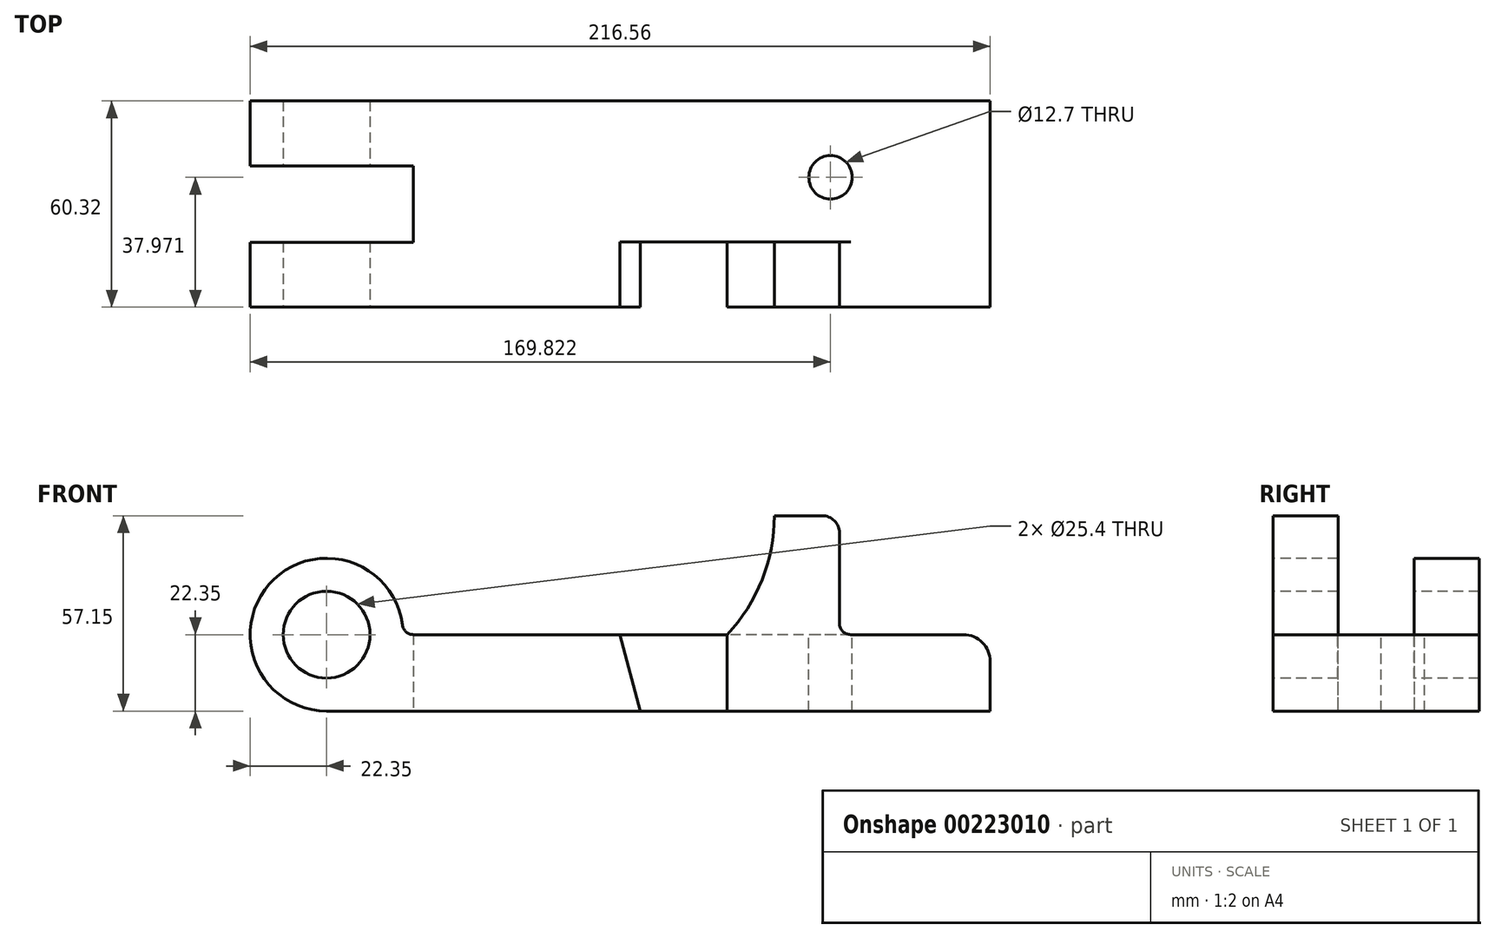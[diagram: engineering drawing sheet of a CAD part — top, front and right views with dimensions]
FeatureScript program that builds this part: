
annotation { "Feature Type Name" : "Feature", "Feature Type Description" : "" }
export const myFeature = defineFeature(function(context is Context, id is Id, definition is map)
    precondition{}
    {
        {
            var Q0;
            Q0=qCreatedBy(makeId("Front.planeOp"),FACE);
            var sketch = newSketch(context, id + "F0", { "sketchPlane" : qUnion([Q0])});
            skCircle(sketch, "E0", {"center": v(0, 0) * mm, "radius": 12.7 * mm});
            skArc(sketch, "E1", {"start": v(22.17, 2.88) * mm, "mid": v(-16.8, 14.75) * mm, "end": v(0, -22.35) * mm});
            skLineSegment(sketch, "E2", {"start": v(0, 0) * mm, "end": v(-22.35, 0) * mm, "construction": true});
            skLineSegment(sketch, "E3", {"start": v(-22.35, 0) * mm, "end": v(-22.35, -22.35) * mm, "construction": true});
            skLineSegment(sketch, "E4", {"start": v(194.2, -22.35) * mm, "end": v(194.2, -7.87) * mm});
            skLineSegment(sketch, "E5", {"start": v(0, 0) * mm, "end": v(0, -22.35) * mm, "construction": true});
            skLineSegment(sketch, "E6", {"start": v(0, -22.35) * mm, "end": v(-22.35, -22.35) * mm, "construction": true});
            skLineSegment(sketch, "E7", {"start": v(0, -22.35) * mm, "end": v(91.85, -22.35) * mm});
            skLineSegment(sketch, "E8", {"start": v(91.85, -22.35) * mm, "end": v(117.25, -22.35) * mm});
            skLineSegment(sketch, "E9", {"start": v(117.25, -22.35) * mm, "end": v(194.2, -22.35) * mm});
            skLineSegment(sketch, "E10", {"start": v(91.85, -22.35) * mm, "end": v(85.85, 0) * mm});
            skLineSegment(sketch, "E11", {"start": v(117.25, -22.35) * mm, "end": v(117.25, 0) * mm});
            skLineSegment(sketch, "E12", {"start": v(186.33, 0) * mm, "end": v(153.4, 0) * mm});
            skLineSegment(sketch, "E13", {"start": v(85.85, 0) * mm, "end": v(25.44, 0) * mm});
            skLineSegment(sketch, "E14", {"start": v(85.85, 0) * mm, "end": v(117.25, 0) * mm});
            skPoint(sketch, "E15.visualSharp", {"position": v(22.35, 0) * mm});
            skArc(sketch, "E15.filletArc", {"start": v(22.17, 2.88) * mm, "mid": v(23.26, 0.82) * mm, "end": v(25.44, 0) * mm});
            skLineSegment(sketch, "E16", {"start": v(0, 0) * mm, "end": v(0, 34.8) * mm, "construction": true});
            skLineSegment(sketch, "E17", {"start": v(0, 34.8) * mm, "end": v(145, 34.8) * mm, "construction": true});
            skLineSegment(sketch, "E18", {"start": v(150.09, 29.72) * mm, "end": v(150.09, 3.3) * mm});
            skLineSegment(sketch, "E19", {"start": v(131.04, 34.8) * mm, "end": v(131.04, 0) * mm, "construction": true});
            skLineSegment(sketch, "E20", {"start": v(150.09, 29.72) * mm, "end": v(150.09, 3.3) * mm, "construction": true});
            skPoint(sketch, "E21.visualSharp", {"position": v(150.09, 34.8) * mm});
            skArc(sketch, "E21.filletArc", {"start": v(150.09, 29.72) * mm, "mid": v(148.6, 33.31) * mm, "end": v(145, 34.8) * mm});
            skPoint(sketch, "E22.newPointA", {"position": v(150.09, -22.35) * mm});
            skArc(sketch, "E22.filletArc", {"start": v(150.09, 3.3) * mm, "mid": v(151.06, 0.97) * mm, "end": v(153.4, 0) * mm});
            skPoint(sketch, "E23.visualSharp", {"position": v(194.2, 0) * mm});
            skArc(sketch, "E23.filletArc", {"start": v(194.2, -7.87) * mm, "mid": v(191.9, -2.3) * mm, "end": v(186.33, 0) * mm});
            skLineSegment(sketch, "E24", {"start": v(153.4, 0) * mm, "end": v(131.04, 0) * mm});
            skLineSegment(sketch, "E25", {"start": v(117.25, 0) * mm, "end": v(131.04, 0) * mm});
            skLineSegment(sketch, "E26", {"start": v(145, 34.8) * mm, "end": v(131.04, 34.8) * mm});
            skLineSegment(sketch, "E27", {"start": v(91.85, -22.35) * mm, "end": v(91.85, 0) * mm, "construction": true});
            skLineSegment(sketch, "E28", {"start": v(25.44, 0) * mm, "end": v(0, 0) * mm, "construction": true});
            skArc(sketch, "E29", {"start": v(117.25, 0) * mm, "mid": v(127.46, 16.08) * mm, "end": v(131.04, 34.8) * mm});
            skLineSegment(sketch, "E30", {"start": v(25.44, 0) * mm, "end": v(25.44, -22.35) * mm});
            skSolve(sketch);
        }
        {
            var Q0;
            Q0=makeQuery(id+"F0.imprint","IMPRINT",FACE,{"disambiguationData":[TD([[makeQuery(id+"F0.imprint","IMPRINT",EDGE,{"derivedFrom":sQuery(id+"F0.wireOp",EDGE,"E0")}),-1.0]])]});
            var Q1;
            Q1=makeQuery(id+"F0.imprint","IMPRINT",FACE,{"disambiguationData":[TD([[makeQuery(id+"F0.imprint","IMPRINT",EDGE,{"derivedFrom":sQuery(id+"F0.wireOp",EDGE,"E4")}),1.0]])]});
            var Q2;
            Q2=makeQuery(id+"F0.imprint","IMPRINT",FACE,{"disambiguationData":[TD([[makeQuery(id+"F0.imprint","IMPRINT",EDGE,{"derivedFrom":sQuery(id+"F0.wireOp",EDGE,"E8")}),1.0]])]});
            var Q3;
            {var subQ0=sQuery(id+"F0.wireOp",EDGE,"E10");Q3=makeQuery(id+"F0.imprint","IMPRINT",FACE,{"disambiguationData":[TD([[makeQuery(id+"F0.imprint","IMPRINT",EDGE,{"derivedFrom":subQ0}),1.0]])]});}
            var Q4;
            {var subQ0=sQuery(id+"F0.wireOp",EDGE,"E30");Q4=makeQuery(id+"F0.imprint","IMPRINT",FACE,{"disambiguationData":[TD([[makeQuery(id+"F0.imprint","IMPRINT",EDGE,{"derivedFrom":subQ0}),1.0]])]});}
            extrude(context, id + "F1", {"entities" : qUnion([Q0, Q1, Q2, Q3, Q4]), "endBound" : BoundingType.SYMMETRIC, "oppositeDirection" : true, "depth" : 60.32 * mm});
        }
        {
            var Q0;
            Q0=makeQuery(id+"F0.imprint","IMPRINT",FACE,{"disambiguationData":[TD([[makeQuery(id+"F0.imprint","IMPRINT",EDGE,{"derivedFrom":sQuery(id+"F0.wireOp",EDGE,"E0")}),-1.0]])]});
            extrude(context, id + "F2", {"entities" : qUnion([Q0]), "operationType" : NewBodyOperationType.REMOVE, "endBound" : BoundingType.SYMMETRIC, "oppositeDirection" : true, "depth" : 22.33 * mm});
        }
        {
            var Q0;
            Q0=makeQuery(id+"F1.opExtrude","CAP_FACE",FACE,{"disambiguationData":[OSD([sQuery(id+"F0.wireOp",EDGE,"E0"),sQuery(id+"F0.wireOp",EDGE,"E1"),sQuery(id+"F0.wireOp",EDGE,"E4"),sQuery(id+"F0.wireOp",EDGE,"E7"),sQuery(id+"F0.wireOp",EDGE,"E8"),sQuery(id+"F0.wireOp",EDGE,"E9"),sQuery(id+"F0.wireOp",EDGE,"E12"),sQuery(id+"F0.wireOp",EDGE,"E13"),sQuery(id+"F0.wireOp",EDGE,"E14"),sQuery(id+"F0.wireOp",EDGE,"E15.filletArc"),sQuery(id+"F0.wireOp",EDGE,"E23.filletArc"),sQuery(id+"F0.wireOp",EDGE,"E24"),sQuery(id+"F0.wireOp",EDGE,"E25")])],"isStart":true});
            var sketch = newSketch(context, id + "F3", { "sketchPlane" : qUnion([Q0])});
            skPoint(sketch, "E31.0", {"position": v(150.09, 16.51) * mm});
            skLineSegment(sketch, "E32.0", {"start": v(150.09, 29.72) * mm, "end": v(150.09, 3.3) * mm});
            skArc(sketch, "E33.0", {"start": v(150.09, 3.3) * mm, "mid": v(151.06, 0.97) * mm, "end": v(153.4, 0) * mm});
            skLineSegment(sketch, "E34.0", {"start": v(153.4, 0) * mm, "end": v(131.04, 0) * mm});
            skLineSegment(sketch, "E35.0", {"start": v(117.25, 0) * mm, "end": v(131.04, 0) * mm});
            skArc(sketch, "E36.0", {"start": v(117.25, 0) * mm, "mid": v(127.46, 16.08) * mm, "end": v(131.04, 34.8) * mm});
            skLineSegment(sketch, "E37.0", {"start": v(145, 34.8) * mm, "end": v(131.04, 34.8) * mm});
            skPoint(sketch, "E38.0", {"position": v(148.6, 33.31) * mm});
            skArc(sketch, "E39.0", {"start": v(150.09, 29.72) * mm, "mid": v(148.6, 33.31) * mm, "end": v(145, 34.8) * mm});
            skLineSegment(sketch, "E40.0", {"start": v(91.85, -22.35) * mm, "end": v(85.85, 0) * mm});
            skLineSegment(sketch, "E41.0", {"start": v(85.85, 0) * mm, "end": v(117.25, 0) * mm});
            skPoint(sketch, "E42.0", {"position": v(117.25, -11.18) * mm});
            skLineSegment(sketch, "E43.0", {"start": v(117.25, -22.35) * mm, "end": v(117.25, 0) * mm});
            skPoint(sketch, "E44.0", {"position": v(101.55, 0) * mm});
            skLineSegment(sketch, "E45.0", {"start": v(91.85, -22.35) * mm, "end": v(117.25, -22.35) * mm});
            skSolve(sketch);
        }
        {
            var Q0;
            Q0 = qSketchRegion(id + "F3", true);
            extrude(context, id + "F4", {"entities" : qUnion([Q0]), "operationType" : NewBodyOperationType.ADD, "oppositeDirection" : true, "depth" : 19.05 * mm});
        }
        {
            var Q0;
            Q0=makeQuery(id+"F3.imprint","IMPRINT",FACE,{"disambiguationData":[TD([[makeQuery(id+"F3.imprint","IMPRINT",EDGE,{"derivedFrom":sQuery(id+"F3.wireOp",EDGE,"E40.0")}),-1.0]])]});
            extrude(context, id + "F5", {"entities" : qUnion([Q0]), "operationType" : NewBodyOperationType.REMOVE, "oppositeDirection" : true, "depth" : 19.05 * mm});
        }
        {
            var Q0;
            Q0=makeQuery(id+"F1.opExtrude","SWEPT_FACE",FACE,{"disambiguationData":[OSD([sQuery(id+"F0.wireOp",EDGE,"E12"),sQuery(id+"F0.wireOp",EDGE,"E13"),sQuery(id+"F0.wireOp",EDGE,"E14"),sQuery(id+"F0.wireOp",EDGE,"E24"),sQuery(id+"F0.wireOp",EDGE,"E25")])]});
            var sketch = newSketch(context, id + "F6", { "sketchPlane" : qUnion([Q0])});
            skCircle(sketch, "E46", {"center": v(147.47, 7.81) * mm, "radius": 6.35 * mm});
            skLineSegment(sketch, "E47.0", {"start": v(186.33, 30.16) * mm, "end": v(25.44, 30.16) * mm, "construction": true});
            skLineSegment(sketch, "E48.0", {"start": v(186.33, 30.16) * mm, "end": v(186.33, -30.16) * mm, "construction": true});
            skLineSegment(sketch, "E49", {"start": v(147.47, 7.81) * mm, "end": v(147.47, 30.16) * mm, "construction": true});
            skLineSegment(sketch, "E50", {"start": v(147.47, 7.81) * mm, "end": v(186.33, 7.81) * mm, "construction": true});
            skSolve(sketch);
        }
        {
            var Q0;
            Q0 = qSketchRegion(id + "F6", true);
            extrude(context, id + "F7", {"entities" : qUnion([Q0]), "operationType" : NewBodyOperationType.REMOVE, "endBound" : BoundingType.THROUGH_ALL, "oppositeDirection" : true, "depth" : 25.4 * mm});
        }
    });
